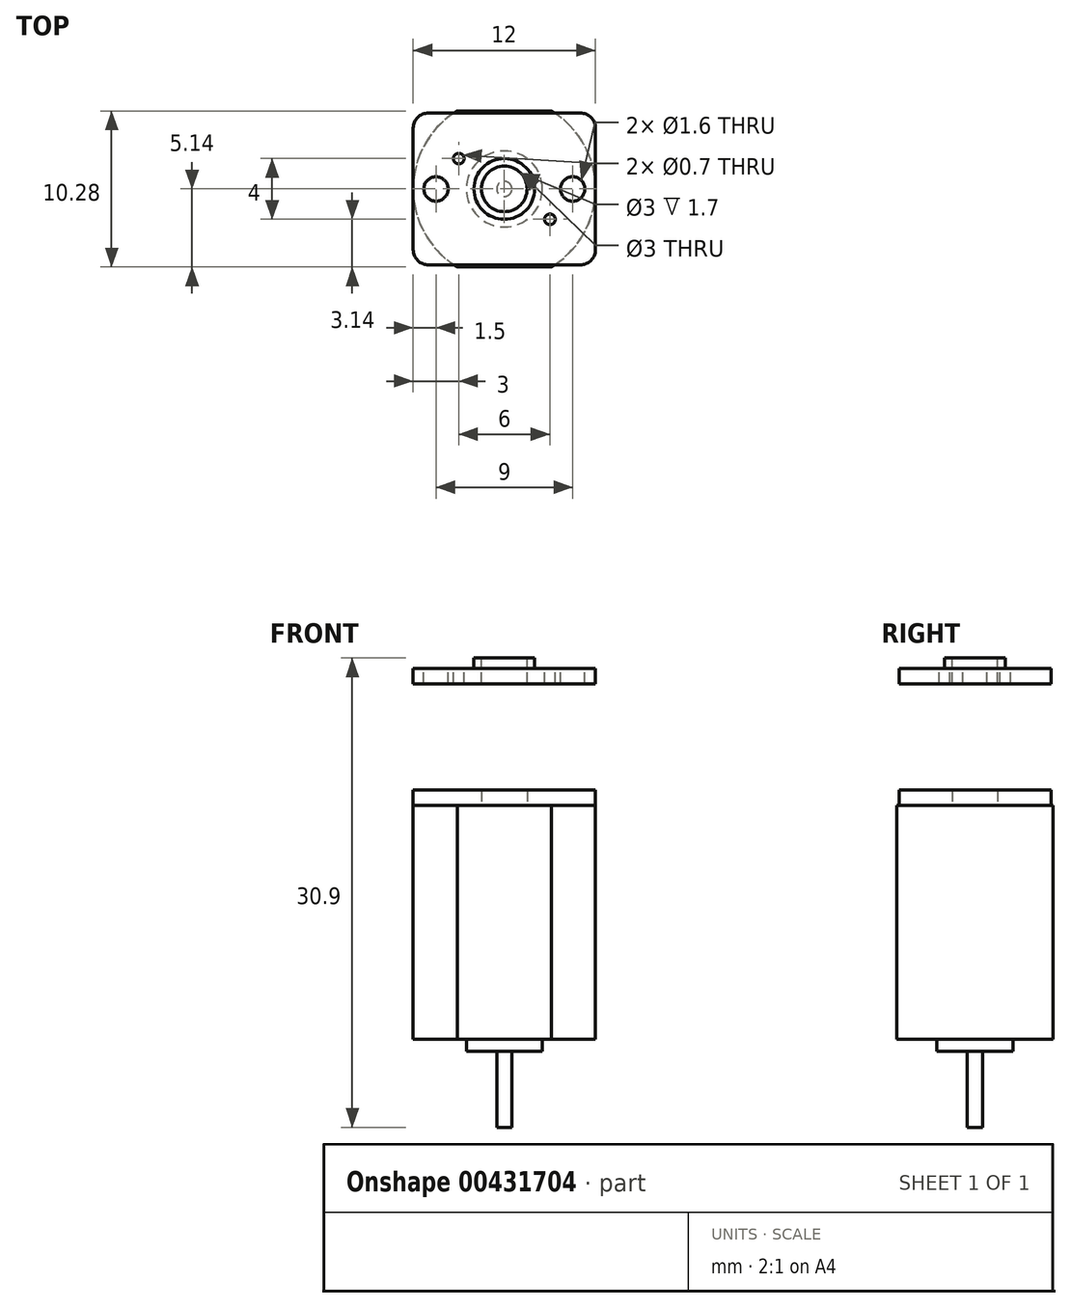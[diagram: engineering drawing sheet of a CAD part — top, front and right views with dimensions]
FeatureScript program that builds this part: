
annotation { "Feature Type Name" : "Feature", "Feature Type Description" : "" }
export const myFeature = defineFeature(function(context is Context, id is Id, definition is map)
    precondition{}
    {
        {
            var Q0;
            Q0=qCreatedBy(makeId("Top.planeOp"),FACE);
            var sketch = newSketch(context, id + "F0", { "sketchPlane" : qUnion([Q0])});
            skArc(sketch, "E0", {"start": v(-3.1, 5.14) * mm, "mid": v(-6, 0) * mm, "end": v(-3.1, -5.14) * mm});
            skLineSegment(sketch, "E1.bottom", {"start": v(-3.1, 5.14) * mm, "end": v(3.1, 5.14) * mm});
            skLineSegment(sketch, "E1.top", {"start": v(-3.1, -5.14) * mm, "end": v(3.1, -5.14) * mm});
            skArc(sketch, "E2.trimOffspring", {"start": v(3.1, -5.14) * mm, "mid": v(6, 0) * mm, "end": v(3.1, 5.14) * mm});
            skSolve(sketch);
        }
        {
            var Q0;
            Q0=makeQuery(id+"F0.imprint","IMPRINT",FACE,{"disambiguationData":[TD([[makeQuery(id+"F0.imprint","IMPRINT",EDGE,{"derivedFrom":sQuery(id+"F0.wireOp",EDGE,"E0")}),1.0]])]});
            extrude(context, id + "F1", {"entities" : qUnion([Q0]), "oppositeDirection" : true, "depth" : 15.4 * mm});
        }
        {
            var Q0;
            Q0=makeQuery(id+"F1.opExtrude","CAP_FACE",FACE,{"disambiguationData":[OSD([sQuery(id+"F0.wireOp",EDGE,"E0"),sQuery(id+"F0.wireOp",EDGE,"E1.bottom"),sQuery(id+"F0.wireOp",EDGE,"E1.top"),sQuery(id+"F0.wireOp",EDGE,"E2.trimOffspring")])],"isStart":false});
            var sketch = newSketch(context, id + "F2", { "sketchPlane" : qUnion([Q0])});
            skCircle(sketch, "E3", {"center": v(0, 0) * mm, "radius": 2.5 * mm});
            skSolve(sketch);
        }
        {
            var Q0;
            Q0=makeQuery(id+"F2.imprint","IMPRINT",FACE,{"disambiguationData":[TD([[makeQuery(id+"F2.imprint","IMPRINT",EDGE,{"derivedFrom":sQuery(id+"F2.wireOp",EDGE,"E3")}),1.0]])]});
            extrude(context, id + "F3", {"entities" : qUnion([Q0]), "operationType" : NewBodyOperationType.ADD, "depth" : .8 * mm});
        }
        {
            var Q0;
            Q0=makeQuery(id+"F3.opExtrude","CAP_FACE",FACE,{"disambiguationData":[OSD([sQuery(id+"F2.wireOp",EDGE,"E3")])],"isStart":false});
            var sketch = newSketch(context, id + "F4", { "sketchPlane" : qUnion([Q0])});
            skCircle(sketch, "E4", {"center": v(0, 0) * mm, "radius": 0.5 * mm});
            skSolve(sketch);
        }
        {
            var Q0;
            Q0=makeQuery(id+"F4.imprint","IMPRINT",FACE,{"disambiguationData":[TD([[makeQuery(id+"F4.imprint","IMPRINT",EDGE,{"derivedFrom":sQuery(id+"F4.wireOp",EDGE,"E4")}),1.0]])]});
            extrude(context, id + "F5", {"entities" : qUnion([Q0]), "operationType" : NewBodyOperationType.ADD, "depth" : 5 * mm});
        }
        {
            var Q0;
            Q0=makeQuery(id+"F1.opExtrude","CAP_FACE",FACE,{"disambiguationData":[OSD([sQuery(id+"F0.wireOp",EDGE,"E0"),sQuery(id+"F0.wireOp",EDGE,"E1.bottom"),sQuery(id+"F0.wireOp",EDGE,"E1.top"),sQuery(id+"F0.wireOp",EDGE,"E2.trimOffspring")])],"isStart":true});
            var sketch = newSketch(context, id + "F6", { "sketchPlane" : qUnion([Q0])});
            skLineSegment(sketch, "E5.bottom", {"start": v(-5, -5) * mm, "end": v(5, -5) * mm});
            skLineSegment(sketch, "E5.top", {"start": v(-5, 5) * mm, "end": v(5, 5) * mm});
            skLineSegment(sketch, "E5.left", {"start": v(-6, -4) * mm, "end": v(-6, 4) * mm});
            skLineSegment(sketch, "E5.right", {"start": v(6, -4) * mm, "end": v(6, 4) * mm});
            skPoint(sketch, "E5.middle", {"position": v(0, 0) * mm});
            skPoint(sketch, "E6.visualSharp", {"position": v(6, 5) * mm});
            skArc(sketch, "E6.filletArc", {"start": v(6, 4) * mm, "mid": v(5.7, 4.7) * mm, "end": v(5, 5) * mm});
            skPoint(sketch, "E7.visualSharp", {"position": v(6, -5) * mm});
            skArc(sketch, "E7.filletArc", {"start": v(5, -5) * mm, "mid": v(5.7, -4.7) * mm, "end": v(6, -4) * mm});
            skPoint(sketch, "E8.visualSharp", {"position": v(-6, -5) * mm});
            skArc(sketch, "E8.filletArc", {"start": v(-6, -4) * mm, "mid": v(-5.7, -4.7) * mm, "end": v(-5, -5) * mm});
            skPoint(sketch, "E9.visualSharp", {"position": v(-6, 5) * mm});
            skArc(sketch, "E9.filletArc", {"start": v(-5, 5) * mm, "mid": v(-5.7, 4.7) * mm, "end": v(-6, 4) * mm});
            skCircle(sketch, "E10", {"center": v(0, 0) * mm, "radius": 1.5 * mm});
            skSolve(sketch);
        }
        {
            var Q0;
            Q0=qSketchRegion(id+"F6",true);
            extrude(context, id + "F7", {"entities" : qUnion([Q0]), "depth" : 1 * mm});
        }
        {
            var Q0;
            Q0=makeQuery(id+"F1.opExtrude","CAP_FACE",FACE,{"disambiguationData":[OSD([sQuery(id+"F0.wireOp",EDGE,"E0"),sQuery(id+"F0.wireOp",EDGE,"E1.bottom"),sQuery(id+"F0.wireOp",EDGE,"E1.top"),sQuery(id+"F0.wireOp",EDGE,"E2.trimOffspring")])],"isStart":true});
            cPlane(context, id + "F8", {"entities" : qUnion([Q0]), "cplaneType" : CPlaneType.OFFSET, "offset" : 9 * mm, "width" : 150 * mm, "height" : 150 * mm});
        }
        {
            var Q0;
            Q0=qCreatedBy(id+"F8.planeOp",FACE);
            var sketch = newSketch(context, id + "F9", { "sketchPlane" : qUnion([Q0])});
            skLineSegment(sketch, "E11.0", {"start": v(-5, -5) * mm, "end": v(5, -5) * mm});
            skArc(sketch, "E12.0", {"start": v(5, -5) * mm, "mid": v(5.7, -4.7) * mm, "end": v(6, -4) * mm});
            skLineSegment(sketch, "E13.0", {"start": v(6, -4) * mm, "end": v(6, 4) * mm});
            skLineSegment(sketch, "E14.0", {"start": v(-6, -4) * mm, "end": v(-6, 4) * mm});
            skArc(sketch, "E15.0", {"start": v(-6, -4) * mm, "mid": v(-5.7, -4.7) * mm, "end": v(-5, -5) * mm});
            skArc(sketch, "E16.0", {"start": v(-5, 5) * mm, "mid": v(-5.7, 4.7) * mm, "end": v(-6, 4) * mm});
            skLineSegment(sketch, "E17.0", {"start": v(-5, 5) * mm, "end": v(5, 5) * mm});
            skArc(sketch, "E18.0", {"start": v(6, 4) * mm, "mid": v(5.7, 4.7) * mm, "end": v(5, 5) * mm});
            skCircle(sketch, "E19.0", {"center": v(0, 0) * mm, "radius": 1.5 * mm});
            skCircle(sketch, "E20", {"center": v(-4.5, 0) * mm, "radius": 0.8 * mm});
            skCircle(sketch, "E21.MirrorC", {"center": v(4.5, 0) * mm, "radius": 0.8 * mm});
            skCircle(sketch, "E22", {"center": v(3, -2) * mm, "radius": 0.35 * mm});
            skLineSegment(sketch, "E23", {"start": v(3, -2) * mm, "end": v(0, 0) * mm, "construction": true});
            skLineSegment(sketch, "E24", {"start": v(0, 0) * mm, "end": v(-3, 2) * mm, "construction": true});
            skCircle(sketch, "E25", {"center": v(-3, 2) * mm, "radius": 0.35 * mm});
            skSolve(sketch);
        }
        {
            var Q0;
            Q0=makeQuery(id+"F9.imprint","IMPRINT",FACE,{"disambiguationData":[TD([[makeQuery(id+"F9.imprint","IMPRINT",EDGE,{"derivedFrom":sQuery(id+"F9.wireOp",EDGE,"E11.0")}),1.0]])]});
            extrude(context, id + "F10", {"entities" : qUnion([Q0]), "oppositeDirection" : true, "depth" : 1 * mm});
        }
        {
            var Q0;
            Q0=makeQuery(id+"F10.opExtrude","CAP_FACE",FACE,{"disambiguationData":[OSD([sQuery(id+"F9.wireOp",EDGE,"E11.0"),sQuery(id+"F9.wireOp",EDGE,"E12.0"),sQuery(id+"F9.wireOp",EDGE,"E13.0"),sQuery(id+"F9.wireOp",EDGE,"E14.0"),sQuery(id+"F9.wireOp",EDGE,"E15.0"),sQuery(id+"F9.wireOp",EDGE,"E16.0"),sQuery(id+"F9.wireOp",EDGE,"E17.0"),sQuery(id+"F9.wireOp",EDGE,"E18.0"),sQuery(id+"F9.wireOp",EDGE,"E19.0"),sQuery(id+"F9.wireOp",EDGE,"E20"),sQuery(id+"F9.wireOp",EDGE,"E21.MirrorC"),sQuery(id+"F9.wireOp",EDGE,"E22"),sQuery(id+"F9.wireOp",EDGE,"E25")])],"isStart":true});
            var sketch = newSketch(context, id + "F11", { "sketchPlane" : qUnion([Q0])});
            skCircle(sketch, "E26", {"center": v(0, 0) * mm, "radius": 2 * mm});
            skCircle(sketch, "E27.0", {"center": v(0, 0) * mm, "radius": 1.5 * mm});
            skSolve(sketch);
        }
        {
            var Q0;
            Q0=makeQuery(id+"F11.imprint","IMPRINT",FACE,{"disambiguationData":[TD([[makeQuery(id+"F11.imprint","IMPRINT",EDGE,{"derivedFrom":sQuery(id+"F11.wireOp",EDGE,"E26")}),1.0]])]});
            extrude(context, id + "F12", {"entities" : qUnion([Q0]), "operationType" : NewBodyOperationType.ADD, "depth" : .7 * mm});
        }
    });
